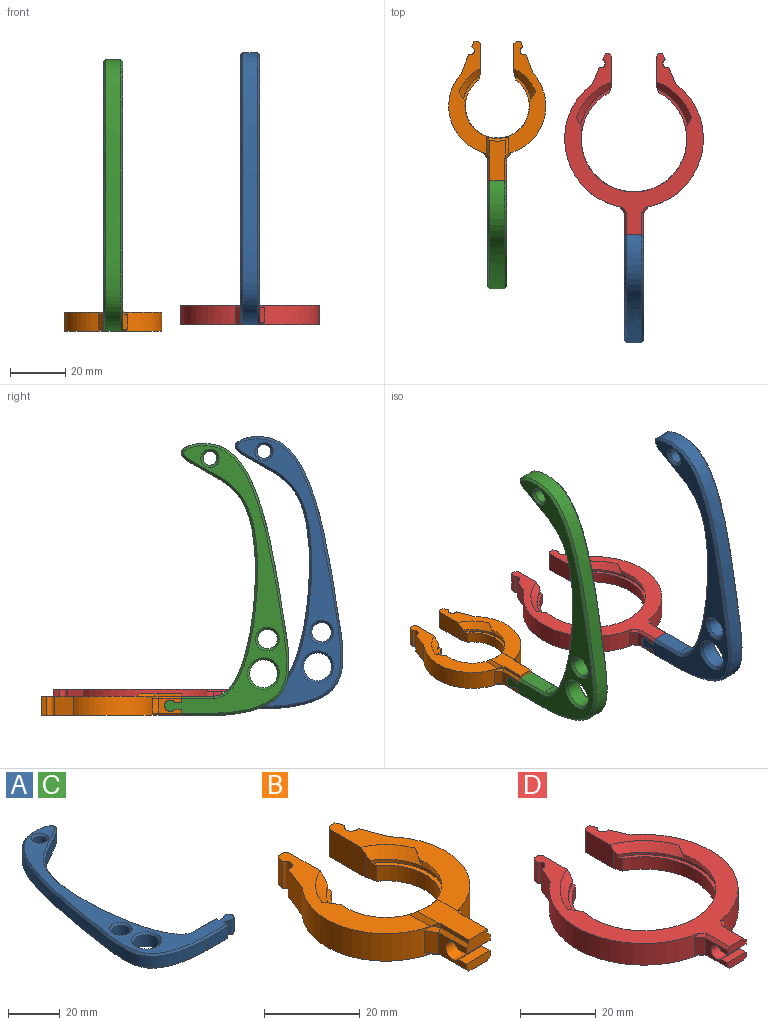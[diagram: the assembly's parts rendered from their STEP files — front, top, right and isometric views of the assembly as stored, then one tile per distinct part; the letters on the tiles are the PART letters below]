
ASSEMBLY  parts=4 mates=2
PART A: 25 faces, bbox 44.8x98.1x7 mm
  f0: cylinder r=2mm len=7mm, axis (0,0,-1), area 69.9mm2, adj f1,f9,f11,f12
  f1: plane 7x2.4mm, normal (0,1,0), area 16.8mm2, adj f0,f2,f11,f12
  f2: plane 7x2.3mm, normal (1,0,0), area 15.5mm2, adj f1,f3,f11,f12,f15,f18
  f3: plane 12x5.4mm, normal (0,1,0), area 64.8mm2, adj f2,f4,f15,f18
  f4: extruded ~97.85x38.45mm, area 1312.6mm2, adj f3,f5,f14,f17
  f5: plane 12x5.4mm, normal (0,-1,0), area 64.8mm2, adj f4,f6,f13,f16
  f6: plane 7x2.3mm, normal (1,0,0), area 15.5mm2, adj f5,f9,f11,f12,f13,f16
  f7: cylinder r=3.5mm len=7mm, axis (0,0,-1), area 118.8mm2, adj f20,f23
  f8: cylinder r=2.5mm len=5.4mm, axis (0,0,-1), area 84.8mm2, adj f21,f24
  f9: plane 7x2.4mm, normal (0,-1,0), area 16.8mm2, adj f0,f6,f11,f12
  f10: cylinder r=5mm len=10mm, axis (0,0,-1), area 169.6mm2, adj f19,f22
  f11: plane 96.5x44.03mm, normal (0,0,1), area 889.5mm2, adj f0,f1,f2,f6,f9,f16,f17,f18
  f12: plane 96.44x44mm, normal (0,0,-1), area 833.8mm2, adj f0,f1,f2,f6,f9,f13,f14,f15
  f13: plane 12x0.8mm, normal (0,-0.71,-0.71), area 13.6mm2, adj f5,f6,f12,f14
  f14: bspline ~98.04x38.84mm, area 272.3mm2, adj f4,f12,f13,f15
  f15: plane 12x0.8mm, normal (0,0.71,-0.71), area 13.6mm2, adj f2,f3,f12,f14
  f16: plane 12x0.8mm, normal (0,-0.71,0.71), area 13.6mm2, adj f5,f6,f11,f17
  f17: bspline ~98.07x38.85mm, area 272.4mm2, adj f4,f11,f16,f18
  f18: plane 12x0.8mm, normal (0,0.71,0.71), area 13.6mm2, adj f2,f3,f11,f17
  f19: cone r=5.8mm half-angle=45deg, axis (0,0,-1), area 38.4mm2, adj f10,f12
  f20: cone r=4.3mm half-angle=45deg, axis (0,0,-1), area 27.7mm2, adj f7,f12
  f21: cone r=3.3mm half-angle=45deg, axis (0,0,-1), area 20.6mm2, adj f8,f12
  f22: cone r=5mm half-angle=45deg, axis (0,0,1), area 38.4mm2, adj f10,f11
  f23: cone r=3.5mm half-angle=45deg, axis (0,0,1), area 27.7mm2, adj f7,f11
  f24: cone r=2.5mm half-angle=45deg, axis (0,0,1), area 20.6mm2, adj f8,f11
PART B: 56 faces, bbox 35.8x51.4x9.1 mm
  f0: plane 41.3x14.35mm, normal (0,0,1), area 206.7mm2, adj f8,f24,f25,f26,f27,f28,f30,f41
  f1: cylinder r=12.5mm len=25mm, axis (0,0,-1), area 52.2mm2, adj f6,f7,f30,f42,f43,f46,f47
  f2: plane 10.47x7.02mm, normal (-1,0,0), area 72.5mm2, adj f3,f4,f42,f45,f46
  f3: plane 41.3x14.35mm, normal (0,0,1), area 206.7mm2, adj f2,f7,f10,f11,f12,f13,f14,f40
  f4: plane 50.59x35mm, normal (0,0,-1), area 588.7mm2, adj f2,f5,f8,f10,f11,f12,f13,f14
  f5: cylinder r=11.5mm len=23mm, axis (0,0,-1), area 232.3mm2, adj f4,f6,f46,f47
  f6: plane 25x23.28mm, normal (0,0,1), area 61.7mm2, adj f1,f5,f46,f47
  f7: bspline ~14.75x12.96mm, area 49.6mm2, adj f1,f3,f30,f40,f54
  f8: plane 10.47x7.02mm, normal (1,0,0), area 72.5mm2, adj f0,f4,f43,f44,f47
  f9: plane 7x3.25mm, normal (0,-1,0), area 20.5mm2, adj f16,f17,f29,f34,f38,f49,f50,f52
  f10: cylinder r=17.5mm len=28.76mm, axis (0,0,-1), area 246.2mm2, adj f3,f4,f11,f23,f33,f35
  f11: plane 7x6.83mm, normal (0.93,0.37,0), area 51.3mm2, adj f3,f4,f10,f12
  f12: cylinder r=1.5mm len=7mm, axis (0,0,-1), area 33mm2, adj f3,f4,f11,f13
  f13: plane 7x2.1mm, normal (0.93,0.37,0), area 15.8mm2, adj f3,f4,f12,f14
  f14: plane 7x1.6mm, normal (0,1,0), area 11.2mm2, adj f3,f4,f13,f45
  f15: plane 7x2.15mm, normal (0,-1,0), area 14.4mm2, adj f4,f16,f18,f29,f32,f36
  f16: plane 8.1x5.4mm, normal (1,0,0), area 24.3mm2, adj f9,f15,f17,f18,f19,f20,f21,f22
  f17: plane 7x2.31mm, normal (0,0,-1), area 16.2mm2, adj f9,f16,f19,f29
  f18: plane 7x2.39mm, normal (0,0,1), area 16.7mm2, adj f15,f16,f20,f29
  f19: cylinder r=2.1mm len=7mm, axis (1,0,0), area 8.7mm2, adj f16,f17,f22,f29
  f20: cylinder r=2.1mm len=7mm, axis (1,0,0), area 54mm2, adj f16,f18,f21,f29
  f21: plane 7x0.7mm, normal (0,-0.6,-0.8), area 6.1mm2, adj f16,f20,f22,f29
  f22: plane 7x0.7mm, normal (0,0.6,-0.8), area 6.1mm2, adj f16,f19,f21,f29
  f23: plane 5.4x2.34mm, normal (0.81,-0.59,0), area 15.7mm2, adj f10,f16,f33,f35
  f24: cylinder r=17.5mm len=28.76mm, axis (0,0,-1), area 246.2mm2, adj f0,f4,f25,f31,f37,f39
  f25: plane 7x6.83mm, normal (-0.93,0.37,0), area 51.3mm2, adj f0,f4,f24,f26
  f26: cylinder r=1.5mm len=7mm, axis (0,0,-1), area 33mm2, adj f0,f4,f25,f27
  f27: plane 7x2.1mm, normal (-0.93,0.37,0), area 15.8mm2, adj f0,f4,f26,f28
  f28: plane 7x1.6mm, normal (0,1,0), area 11.2mm2, adj f0,f4,f27,f44
  f29: plane 8.1x5.4mm, normal (-1,0,0), area 24.3mm2, adj f9,f15,f17,f18,f19,f20,f21,f22
  f30: bspline ~14.75x12.96mm, area 48.4mm2, adj f0,f1,f7,f41,f54
  f31: plane 5.4x2.34mm, normal (-0.81,-0.59,0), area 15.7mm2, adj f24,f29,f37,f39
  f32: plane 8.37x0.8mm, normal (0.71,0,-0.71), area 9.3mm2, adj f4,f15,f16,f33
  f33: plane 2.54x2.36mm, normal (0.57,-0.42,-0.71), area 2.8mm2, adj f4,f10,f23,f32
  f34: plane 8.37x0.8mm, normal (0.71,0,0.71), area 9.3mm2, adj f9,f16,f35,f50
  f35: plane 2.54x2.36mm, normal (0.57,-0.42,0.71), area 2.8mm2, adj f10,f23,f34,f51
  f36: plane 8.37x0.8mm, normal (-0.71,0,-0.71), area 9.3mm2, adj f4,f15,f29,f37
  f37: plane 2.54x2.36mm, normal (-0.57,-0.42,-0.71), area 2.8mm2, adj f4,f24,f31,f36
  f38: plane 8.37x0.8mm, normal (-0.71,0,0.71), area 9.3mm2, adj f9,f29,f39,f49
  f39: plane 2.54x2.36mm, normal (-0.57,-0.42,0.71), area 2.8mm2, adj f24,f31,f38,f48
  f40: bspline ~3.74x3.68mm, area 4.7mm2, adj f3,f7,f42
  f41: bspline ~3.71x3.67mm, area 4.7mm2, adj f0,f30,f43
  f42: cone r=14.7mm half-angle=45deg, axis (0,0,1), area 35.9mm2, adj f1,f2,f3,f40,f46
  f43: cone r=14.7mm half-angle=45deg, axis (0,0,1), area 35.9mm2, adj f0,f1,f8,f41,f47
  f44: plane 7x0.8mm, normal (0.71,0.71,0), area 7.9mm2, adj f0,f4,f8,f28
  f45: plane 7x0.8mm, normal (-0.71,0.71,0), area 7.9mm2, adj f2,f3,f4,f14
  f46: plane 5.93x2.85mm, normal (-0.97,-0.22,0), area 13.4mm2, adj f1,f2,f4,f5,f6,f42
  f47: plane 5.93x2.85mm, normal (0.97,-0.22,0), area 13.4mm2, adj f1,f4,f5,f6,f8,f43
  f48: plane 1.74x1.28mm, normal (-0.81,-0.59,0), area 1.3mm2, adj f39,f49,f52,f55
  f49: plane 8.37x1mm, normal (-1,0,0), area 8.4mm2, adj f9,f38,f48,f52
  f50: plane 8.37x1mm, normal (1,0,0), area 8.4mm2, adj f9,f34,f51,f52
  f51: plane 1.74x1.28mm, normal (0.81,-0.59,0), area 1.3mm2, adj f35,f50,f52,f53
  f52: plane 14.87x5.95mm, normal (0,0,1), area 82.4mm2, adj f9,f48,f49,f50,f51,f53,f54,f55
  f53: plane 7.52x1.05mm, normal (0.71,0,0.71), area 8.6mm2, adj f3,f51,f52,f54
  f54: cone r=12.63mm half-angle=45deg, axis (0,0,1), area 10mm2, adj f7,f30,f52,f53,f55
  f55: plane 7.52x1.05mm, normal (-0.71,0,0.71), area 8.6mm2, adj f0,f48,f52,f54
PART C: same geometry as A
PART D: 47 faces, bbox 67x65.5x8.3 mm
  f0: cylinder r=20mm len=40mm, axis (0,0,-1), area 86.7mm2, adj f5,f6,f29,f41,f42,f45,f46
  f1: plane 10.66x7.02mm, normal (-1,0,0), area 73.5mm2, adj f2,f3,f41,f44,f45
  f2: plane 65.44x50mm, normal (0,0,1), area 727.1mm2, adj f1,f6,f7,f8,f9,f10,f11,f12
  f3: plane 65.44x50mm, normal (0,0,-1), area 848.1mm2, adj f1,f4,f7,f9,f10,f11,f12,f13
  f4: cylinder r=19mm len=38mm, axis (0,0,-1), area 403.8mm2, adj f3,f5,f45,f46
  f5: plane 40x38.16mm, normal (0,0,1), area 104.7mm2, adj f0,f4,f45,f46
  f6: bspline ~38.33x33.88mm, area 83.6mm2, adj f0,f2,f29,f39
  f7: plane 10.66x7.02mm, normal (1,0,0), area 73.5mm2, adj f2,f3,f42,f43,f46
  f8: plane 7x2.25mm, normal (0,-1,0), area 15.1mm2, adj f2,f15,f16,f28,f33,f37
  f9: cylinder r=25mm len=44.66mm, axis (0,0,-1), area 400.7mm2, adj f2,f3,f10,f22,f32,f34
  f10: plane 7x5.81mm, normal (0.92,0.4,0), area 44.3mm2, adj f2,f3,f9,f11
  f11: cylinder r=1.5mm len=7mm, axis (0,0,-1), area 33mm2, adj f2,f3,f10,f12
  f12: plane 7x2.12mm, normal (0.92,0.4,0), area 16.2mm2, adj f2,f3,f11,f13
  f13: plane 7x1.6mm, normal (0,1,0), area 11.2mm2, adj f2,f3,f12,f44
  f14: plane 7x2.15mm, normal (0,-1,0), area 14.4mm2, adj f3,f15,f17,f28,f31,f35
  f15: plane 8.08x5.4mm, normal (1,0,0), area 24.2mm2, adj f8,f14,f16,f17,f18,f19,f20,f21
  f16: plane 7x2.31mm, normal (0,0,-1), area 16.2mm2, adj f8,f15,f18,f28
  f17: plane 7x2.39mm, normal (0,0,1), area 16.7mm2, adj f14,f15,f19,f28
  f18: cylinder r=2.1mm len=7mm, axis (1,0,0), area 8.7mm2, adj f15,f16,f21,f28
  f19: cylinder r=2.1mm len=7mm, axis (1,0,0), area 54mm2, adj f15,f17,f20,f28
  f20: plane 7x0.7mm, normal (0,-0.6,-0.8), area 6.1mm2, adj f15,f19,f21,f28
  f21: plane 7x0.7mm, normal (0,0.6,-0.8), area 6.1mm2, adj f15,f18,f20,f28
  f22: plane 5.4x2.25mm, normal (0.78,-0.63,0), area 15.6mm2, adj f9,f15,f32,f34
  f23: cylinder r=25mm len=44.66mm, axis (0,0,-1), area 400.7mm2, adj f2,f3,f24,f30,f36,f38
  f24: plane 7x5.81mm, normal (-0.92,0.4,0), area 44.3mm2, adj f2,f3,f23,f25
  f25: cylinder r=1.5mm len=7mm, axis (0,0,-1), area 33mm2, adj f2,f3,f24,f26
  f26: plane 7x2.12mm, normal (-0.92,0.4,0), area 16.2mm2, adj f2,f3,f25,f27
  f27: plane 7x1.6mm, normal (0,1,0), area 11.2mm2, adj f2,f3,f26,f43
  f28: plane 8.08x5.4mm, normal (-1,0,0), area 24.2mm2, adj f8,f14,f16,f17,f18,f19,f20,f21
  f29: bspline ~38.33x34.5mm, area 82.6mm2, adj f0,f2,f6,f40
  f30: plane 5.4x2.25mm, normal (-0.78,-0.63,0), area 15.6mm2, adj f23,f28,f36,f38
  f31: plane 8.36x0.8mm, normal (0.71,0,-0.71), area 9.3mm2, adj f3,f14,f15,f32
  f32: plane 2.62x2.26mm, normal (0.55,-0.44,-0.71), area 2.9mm2, adj f3,f9,f22,f31
  f33: plane 8.36x0.8mm, normal (0.71,0,0.71), area 9.3mm2, adj f2,f8,f15,f34
  f34: plane 2.62x2.26mm, normal (0.55,-0.44,0.71), area 2.9mm2, adj f2,f9,f22,f33
  f35: plane 8.36x0.8mm, normal (-0.71,0,-0.71), area 9.3mm2, adj f3,f14,f28,f36
  f36: plane 2.62x2.26mm, normal (-0.55,-0.44,-0.71), area 2.9mm2, adj f3,f23,f30,f35
  f37: plane 8.36x0.8mm, normal (-0.71,0,0.71), area 9.3mm2, adj f2,f8,f28,f38
  f38: plane 2.62x2.26mm, normal (-0.55,-0.44,0.71), area 2.9mm2, adj f2,f23,f30,f37
  f39: bspline ~3.86x3.68mm, area 4.8mm2, adj f2,f6,f41
  f40: bspline ~3.79x3.37mm, area 4.8mm2, adj f2,f29,f42
  f41: cone r=22.2mm half-angle=45deg, axis (0,0,1), area 58.6mm2, adj f0,f1,f2,f39,f45
  f42: cone r=22.2mm half-angle=45deg, axis (0,0,1), area 58.6mm2, adj f0,f2,f7,f40,f46
  f43: plane 7x0.8mm, normal (0.71,0.71,0), area 7.9mm2, adj f2,f3,f7,f27
  f44: plane 7x0.8mm, normal (-0.71,0.71,0), area 7.9mm2, adj f1,f2,f3,f13
  f45: plane 5.66x2.45mm, normal (-0.94,-0.33,0), area 11.7mm2, adj f0,f1,f3,f4,f5,f41
  f46: plane 5.66x2.45mm, normal (0.94,-0.33,0), area 11.7mm2, adj f0,f3,f4,f5,f7,f42
PLACE A rot(axis=(0.58,0.58,0.58),120deg) t=(48.54,-35.07,11.14)mm
PLACE B t=(2.74,11.56,8.65)mm fixed
PLACE C rot(axis=(0.58,0.58,0.58),120deg) t=(-0.76,-15.59,8.65)mm
PLACE D t=(52.04,-0.31,11.14)mm
MATE fastened C.f0 <-> B.f19  axis (1,0,0) through (6.24,-11.59,12.15)mm
MATE fastened A.f0 <-> D.f18  axis (1,0,0) through (55.54,-31.07,14.64)mm
